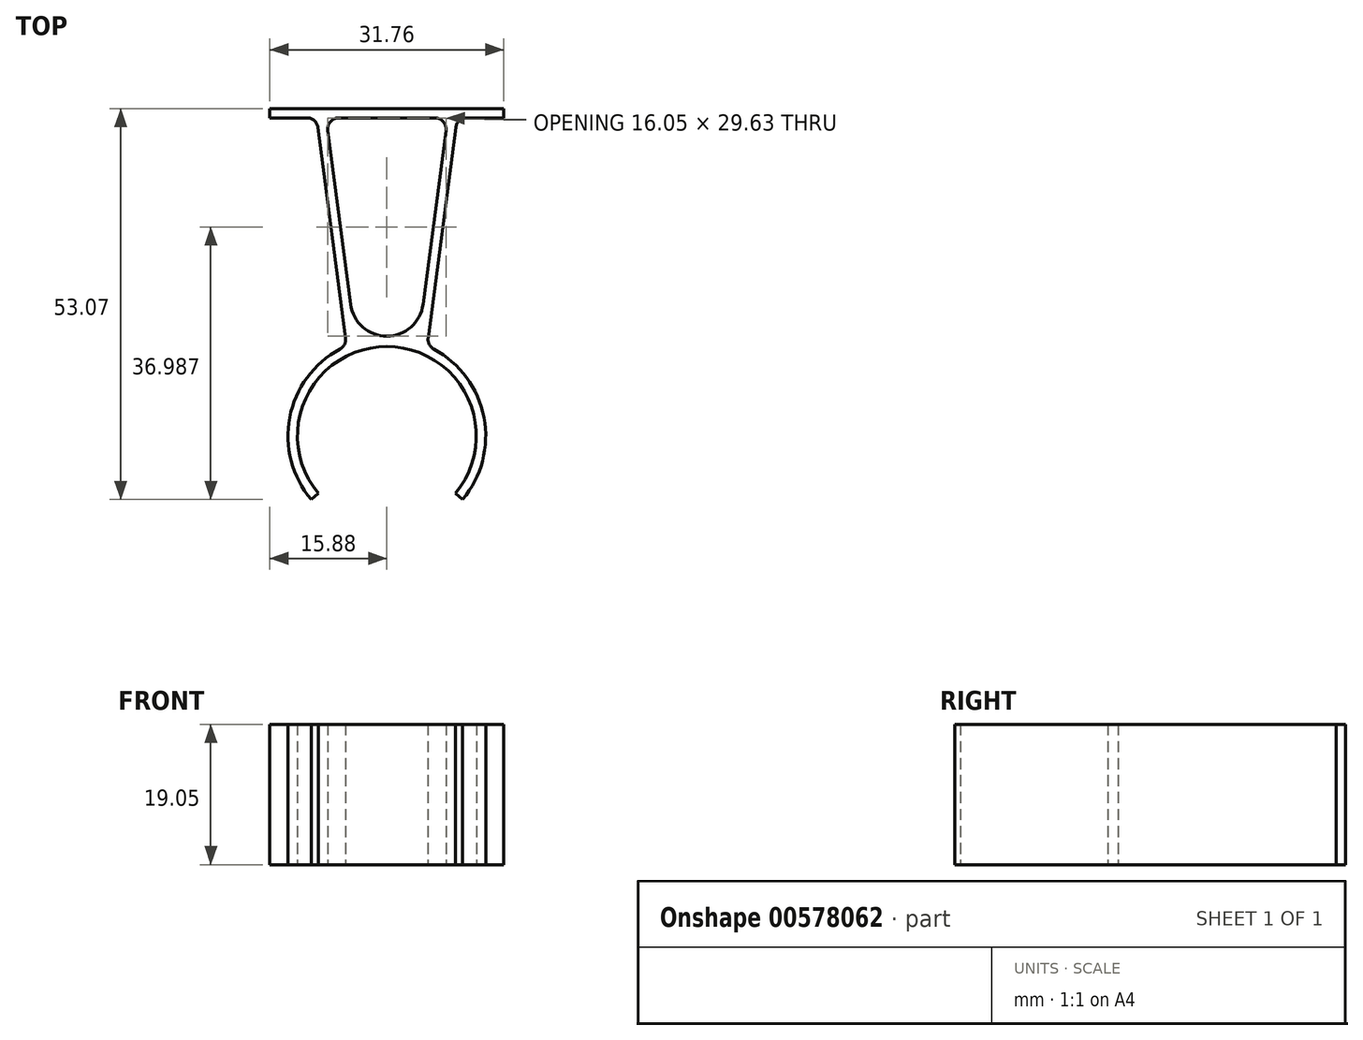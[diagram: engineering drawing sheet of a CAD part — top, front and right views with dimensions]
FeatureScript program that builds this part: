
annotation { "Feature Type Name" : "Feature", "Feature Type Description" : "" }
export const myFeature = defineFeature(function(context is Context, id is Id, definition is map)
    precondition{}
    {
        {
            var Q0;
            Q0=qCreatedBy(makeId("Top.planeOp"),FACE);
            var sketch = newSketch(context, id + "F0", { "sketchPlane" : qUnion([Q0])});
            skArc(sketch, "E0", {"start": v(9.3, -7.8) * mm, "mid": v(0, 12.14) * mm, "end": v(-9.3, -7.8) * mm});
            skArc(sketch, "E1", {"start": v(-6.38, 11.8) * mm, "mid": v(-13.17, 2.51) * mm, "end": v(-10.27, -8.62) * mm});
            skLineSegment(sketch, "E2", {"start": v(-5.6, 13.33) * mm, "end": v(-9.35, 41.85) * mm});
            skLineSegment(sketch, "E3", {"start": v(-10.86, 43.18) * mm, "end": v(-15.88, 43.18) * mm});
            skLineSegment(sketch, "E4", {"start": v(-15.88, 43.18) * mm, "end": v(-15.88, 44.45) * mm});
            skLineSegment(sketch, "E5", {"start": v(-15.88, 44.45) * mm, "end": v(15.88, 44.45) * mm});
            skLineSegment(sketch, "E6", {"start": v(15.88, 44.45) * mm, "end": v(15.88, 43.18) * mm});
            skLineSegment(sketch, "E7", {"start": v(15.88, 43.18) * mm, "end": v(10.86, 43.18) * mm});
            skLineSegment(sketch, "E8", {"start": v(9.35, 41.85) * mm, "end": v(5.6, 13.33) * mm});
            skLineSegment(sketch, "E9", {"start": v(-6.5, 43.18) * mm, "end": v(6.5, 43.18) * mm});
            skLineSegment(sketch, "E10", {"start": v(8.02, 41.46) * mm, "end": v(4.91, 17.86) * mm});
            skLineSegment(sketch, "E11", {"start": v(-4.91, 17.86) * mm, "end": v(-8.02, 41.46) * mm});
            skLineSegment(sketch, "E12", {"start": v(-10.27, -8.62) * mm, "end": v(-9.3, -7.8) * mm});
            skLineSegment(sketch, "E13", {"start": v(9.3, -7.8) * mm, "end": v(10.27, -8.62) * mm});
            skArc(sketch, "E14.trimOffspring", {"start": v(10.27, -8.62) * mm, "mid": v(13.17, 2.51) * mm, "end": v(6.38, 11.8) * mm});
            skLineSegment(sketch, "E15", {"start": v(0, 0) * mm, "end": v(0, 44.45) * mm, "construction": true});
            skPoint(sketch, "E16.visualSharp", {"position": v(-5.45, 12.25) * mm});
            skArc(sketch, "E16.filletArc", {"start": v(-6.38, 11.8) * mm, "mid": v(-5.75, 12.44) * mm, "end": v(-5.6, 13.33) * mm});
            skPoint(sketch, "E17.visualSharp", {"position": v(5.45, 12.25) * mm});
            skArc(sketch, "E17.filletArc", {"start": v(5.6, 13.33) * mm, "mid": v(5.75, 12.44) * mm, "end": v(6.38, 11.8) * mm});
            skPoint(sketch, "E18.visualSharp", {"position": v(-9.53, 43.18) * mm});
            skArc(sketch, "E18.filletArc", {"start": v(-9.35, 41.85) * mm, "mid": v(-9.86, 42.8) * mm, "end": v(-10.86, 43.18) * mm});
            skPoint(sketch, "E19.visualSharp", {"position": v(9.52, 43.18) * mm});
            skArc(sketch, "E19.filletArc", {"start": v(10.86, 43.18) * mm, "mid": v(9.86, 42.8) * mm, "end": v(9.35, 41.85) * mm});
            skPoint(sketch, "E20.visualSharp", {"position": v(-8.24, 43.18) * mm});
            skArc(sketch, "E20.filletArc", {"start": v(-6.5, 43.18) * mm, "mid": v(-7.65, 42.66) * mm, "end": v(-8.02, 41.46) * mm});
            skPoint(sketch, "E21.visualSharp", {"position": v(8.24, 43.18) * mm});
            skArc(sketch, "E21.filletArc", {"start": v(8.02, 41.46) * mm, "mid": v(7.65, 42.66) * mm, "end": v(6.5, 43.18) * mm});
            skPoint(sketch, "E22.visualSharp", {"position": v(0, -19.44) * mm});
            skArc(sketch, "E22.filletArc", {"start": v(-4.91, 17.86) * mm, "mid": v(0, 13.55) * mm, "end": v(4.91, 17.86) * mm});
            skSolve(sketch);
        }
        {
            var Q0;
            Q0 = qSketchRegion(id + "F0", true);
            extrude(context, id + "F1", {"entities" : qUnion([Q0]), "depth" : 19.05 * mm, "offsetDistance" : 25.4 * mm});
        }
    });
